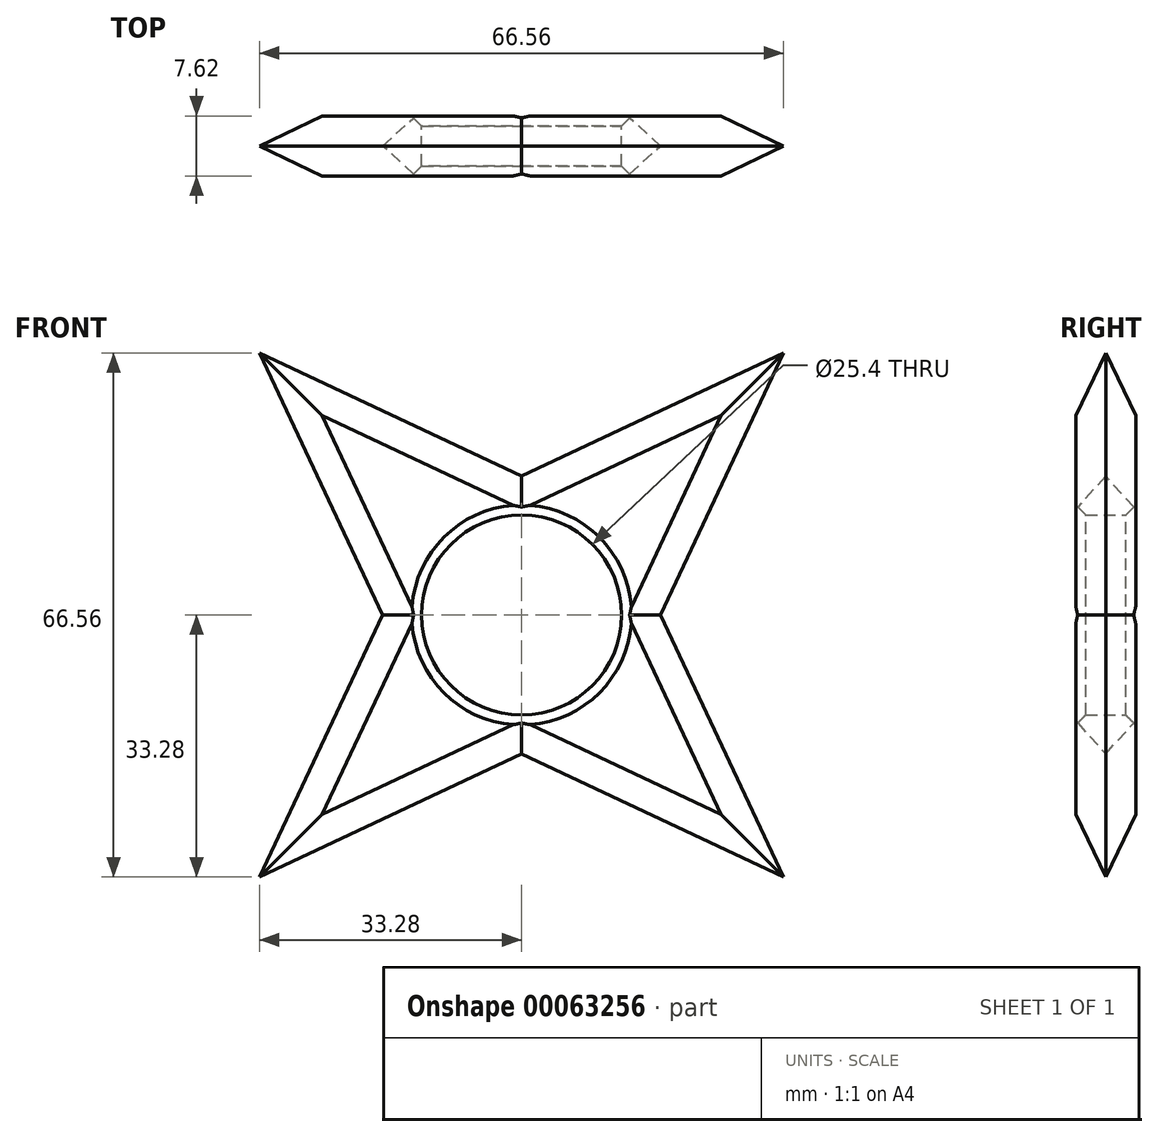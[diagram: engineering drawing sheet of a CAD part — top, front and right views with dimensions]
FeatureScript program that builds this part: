
annotation { "Feature Type Name" : "Feature", "Feature Type Description" : "" }
export const myFeature = defineFeature(function(context is Context, id is Id, definition is map)
    precondition{}
    {
        {
            var Q0;
            Q0=qCreatedBy(makeId("Front.planeOp"),FACE);
            var sketch = newSketch(context, id + "F0", { "sketchPlane" : qUnion([Q0])});
            skCircle(sketch, "E0", {"center": v(0, 0) * mm, "radius": 12.7 * mm});
            skLineSegment(sketch, "E1", {"start": v(-35.92, -35.92) * mm, "end": v(0, -19.05) * mm});
            skLineSegment(sketch, "E2", {"start": v(0, -19.05) * mm, "end": v(35.92, -35.92) * mm});
            skLineSegment(sketch, "E3", {"start": v(35.92, -35.92) * mm, "end": v(19.05, 0) * mm});
            skLineSegment(sketch, "E4", {"start": v(19.05, 0) * mm, "end": v(35.92, 35.92) * mm});
            skLineSegment(sketch, "E5", {"start": v(35.92, 35.92) * mm, "end": v(0, 19.05) * mm});
            skLineSegment(sketch, "E6", {"start": v(0, 19.05) * mm, "end": v(-35.92, 35.92) * mm});
            skLineSegment(sketch, "E7", {"start": v(-35.92, 35.92) * mm, "end": v(-19.05, 0) * mm});
            skLineSegment(sketch, "E8", {"start": v(-19.05, 0) * mm, "end": v(-35.92, -35.92) * mm});
            skSolve(sketch);
        }
        {
            var Q0;
            Q0=makeQuery(id+"F0.imprint","IMPRINT",FACE,{"disambiguationData":[TD([[makeQuery(id+"F0.imprint","IMPRINT",EDGE,{"derivedFrom":sQuery(id+"F0.wireOp",EDGE,"E0")}),-1.0]])]});
            extrude(context, id + "F1", {"entities" : qUnion([Q0]), "depth" : 7.62 * mm});
        }
        {
            var Q0;
            Q0=makeQuery(id+"F1.opExtrude","CAP_EDGE",EDGE,{"disambiguationData":[OSD([sQuery(id+"F0.wireOp",EDGE,"E0")])],"isStart":false});
            chamfer(context, id + "F2", {"entities" : qUnion([Q0]), "width" : 1.27 * mm, "tangentPropagation" : true});
        }
        {
            var Q0;
            Q0=makeQuery(id+"F1.opExtrude","CAP_EDGE",EDGE,{"disambiguationData":[OSD([sQuery(id+"F0.wireOp",EDGE,"E0")])],"isStart":true});
            chamfer(context, id + "F3", {"entities" : qUnion([Q0]), "width" : 1.27 * mm, "tangentPropagation" : true});
        }
        {
            var Q0;
            Q0=makeQuery(id+"F1.opExtrude","CAP_EDGE",EDGE,{"disambiguationData":[OSD([sQuery(id+"F0.wireOp",EDGE,"E5")])],"isStart":false});
            chamfer(context, id + "F4", {"entities" : qUnion([Q0]), "width" : 5.08 * mm, "tangentPropagation" : true});
        }
        {
            var Q0;
            Q0=makeQuery(id+"F1.opExtrude","CAP_EDGE",EDGE,{"disambiguationData":[OSD([sQuery(id+"F0.wireOp",EDGE,"E5")])],"isStart":true});
            chamfer(context, id + "F5", {"entities" : qUnion([Q0]), "width" : 5.08 * mm, "tangentPropagation" : true});
        }
        {
            var Q0;
            Q0=makeQuery(id+"F1.opExtrude","CAP_EDGE",EDGE,{"disambiguationData":[OSD([sQuery(id+"F0.wireOp",EDGE,"E4")])],"isStart":false});
            chamfer(context, id + "F6", {"entities" : qUnion([Q0]), "width" : 5.08 * mm, "tangentPropagation" : true});
        }
        {
            var Q0;
            Q0=makeQuery(id+"F1.opExtrude","CAP_EDGE",EDGE,{"disambiguationData":[OSD([sQuery(id+"F0.wireOp",EDGE,"E4")])],"isStart":true});
            chamfer(context, id + "F7", {"entities" : qUnion([Q0]), "width" : 5.08 * mm, "tangentPropagation" : true});
        }
        {
            var Q0;
            Q0=makeQuery(id+"F1.opExtrude","CAP_EDGE",EDGE,{"disambiguationData":[OSD([sQuery(id+"F0.wireOp",EDGE,"E3")])],"isStart":false});
            chamfer(context, id + "F8", {"entities" : qUnion([Q0]), "width" : 5.08 * mm, "tangentPropagation" : true});
        }
        {
            var Q0;
            Q0=makeQuery(id+"F1.opExtrude","CAP_EDGE",EDGE,{"disambiguationData":[OSD([sQuery(id+"F0.wireOp",EDGE,"E3")])],"isStart":true});
            chamfer(context, id + "F9", {"entities" : qUnion([Q0]), "width" : 5.08 * mm, "tangentPropagation" : true});
        }
        {
            var Q0;
            Q0=makeQuery(id+"F1.opExtrude","CAP_EDGE",EDGE,{"disambiguationData":[OSD([sQuery(id+"F0.wireOp",EDGE,"E2")])],"isStart":false});
            chamfer(context, id + "F10", {"entities" : qUnion([Q0]), "width" : 5.08 * mm, "tangentPropagation" : true});
        }
        {
            var Q0;
            Q0=makeQuery(id+"F1.opExtrude","CAP_EDGE",EDGE,{"disambiguationData":[OSD([sQuery(id+"F0.wireOp",EDGE,"E2")])],"isStart":true});
            chamfer(context, id + "F11", {"entities" : qUnion([Q0]), "width" : 5.08 * mm, "tangentPropagation" : true});
        }
        {
            var Q0;
            Q0=makeQuery(id+"F1.opExtrude","CAP_EDGE",EDGE,{"disambiguationData":[OSD([sQuery(id+"F0.wireOp",EDGE,"E1")])],"isStart":true});
            chamfer(context, id + "F12", {"entities" : qUnion([Q0]), "width" : 5.08 * mm, "tangentPropagation" : true});
        }
        {
            var Q0;
            Q0=makeQuery(id+"F1.opExtrude","CAP_EDGE",EDGE,{"disambiguationData":[OSD([sQuery(id+"F0.wireOp",EDGE,"E1")])],"isStart":false});
            chamfer(context, id + "F13", {"entities" : qUnion([Q0]), "width" : 5.08 * mm, "tangentPropagation" : true});
        }
        {
            var Q0;
            Q0=makeQuery(id+"F1.opExtrude","CAP_EDGE",EDGE,{"disambiguationData":[OSD([sQuery(id+"F0.wireOp",EDGE,"E8")])],"isStart":false});
            chamfer(context, id + "F14", {"entities" : qUnion([Q0]), "width" : 5.08 * mm, "tangentPropagation" : true});
        }
        {
            var Q0;
            Q0=makeQuery(id+"F1.opExtrude","CAP_EDGE",EDGE,{"disambiguationData":[OSD([sQuery(id+"F0.wireOp",EDGE,"E8")])],"isStart":true});
            chamfer(context, id + "F15", {"entities" : qUnion([Q0]), "width" : 5.08 * mm, "tangentPropagation" : true});
        }
        {
            var Q0;
            Q0=makeQuery(id+"F1.opExtrude","CAP_EDGE",EDGE,{"disambiguationData":[OSD([sQuery(id+"F0.wireOp",EDGE,"E7")])],"isStart":false});
            chamfer(context, id + "F16", {"entities" : qUnion([Q0]), "width" : 5.08 * mm, "tangentPropagation" : true});
        }
        {
            var Q0;
            Q0=makeQuery(id+"F1.opExtrude","CAP_EDGE",EDGE,{"disambiguationData":[OSD([sQuery(id+"F0.wireOp",EDGE,"E7")])],"isStart":true});
            chamfer(context, id + "F17", {"entities" : qUnion([Q0]), "width" : 5.08 * mm, "tangentPropagation" : true});
        }
        {
            var Q0;
            Q0=makeQuery(id+"F1.opExtrude","CAP_EDGE",EDGE,{"disambiguationData":[OSD([sQuery(id+"F0.wireOp",EDGE,"E6")])],"isStart":false});
            chamfer(context, id + "F18", {"entities" : qUnion([Q0]), "width" : 5.08 * mm, "tangentPropagation" : true});
        }
        {
            var Q0;
            Q0=makeQuery(id+"F1.opExtrude","CAP_EDGE",EDGE,{"disambiguationData":[OSD([sQuery(id+"F0.wireOp",EDGE,"E6")])],"isStart":true});
            chamfer(context, id + "F19", {"entities" : qUnion([Q0]), "width" : 5.08 * mm, "tangentPropagation" : true});
        }
    });
